# Revit family: 7418 Leros Trimless
name_source: partatom
category: Lighting Fixtures
revit_build: Autodesk Revit 2018 (Build: 20170223_1515(x64)
units: mm (PartAtom-declared; Revit-internal decimal feet)

## family parameters
Always vertical = Yes
Cut with Voids When Loaded = No
Host = Wall
Light Source = Yes
OmniClass Number = 23.80.70.00
OmniClass Title = Lighting
Part Type = Normal
Room Calculation Point = No
Round Connector Dimension = Use Diameter
Shared = No

## types (2) — shared parameters
ADA compliant = Not Applicable
Color Filter = 16777215
Dimmable = Yes
Dimming Lamp Color Temperature Shift = <None>
Dimming Method = Control Gear Dependent
Driver Included = No
Driver Required = Constant Current 350mA
Efficacy (lm/w) = 32.36
Lamp = LED
Light Source Fixed = Yes
Main Finish = Matt White
Main Material = Metal - Zinc
Manufacturer = Astro Lighting Ltd
Power (Watts) = 1x 1W LED
Product Code = 7418
Product Location = Interior
Product Name = Leros Trimless LED
Product SKU = 1342002
URL = www.astrolighting.com

## per-type parameters (varying)
| type | Electrical Class | Location rating | Photometric Web File | Tilt Angle |
| Astro Leros Trimless LED (CE) | 3 | IP20 | 7418_XPE-2700K_170801.ies | 90.00° |
| Astro Leros Trimless LED (UL) | 2 | Dry | 1342002_Leros Trimless LED_Photometry_IES_Iss. 01.ies | 60.00° |

## geometry (parser evidence)
native form markers: Sweep x1
no freeform markers — native parametric forms only
